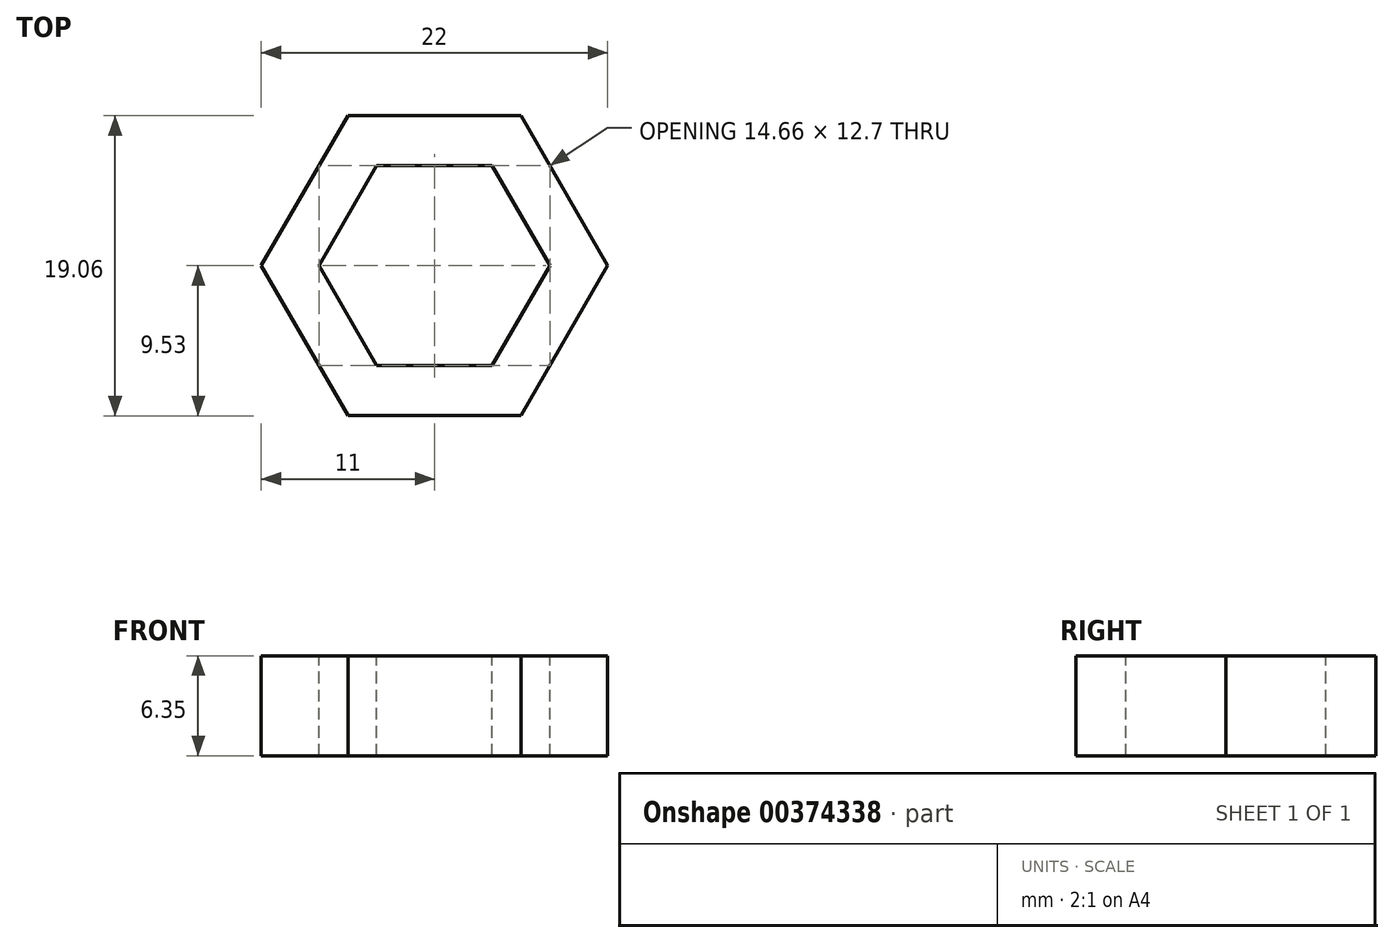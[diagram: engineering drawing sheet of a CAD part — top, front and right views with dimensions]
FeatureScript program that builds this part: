
annotation { "Feature Type Name" : "Feature", "Feature Type Description" : "" }
export const myFeature = defineFeature(function(context is Context, id is Id, definition is map)
    precondition{}
    {
        {
            var Q0;
            Q0=qCreatedBy(makeId("Top.planeOp"),FACE);
            cPlane(context, id + "F0", {"entities" : qUnion([Q0]), "cplaneType" : CPlaneType.OFFSET, "offset" : 38.1 * mm, "width" : 152.4 * mm, "height" : 152.4 * mm});
        }
        {
            var Q0;
            Q0=qCreatedBy(id+"F0.planeOp",FACE);
            var sketch = newSketch(context, id + "F1", { "sketchPlane" : qUnion([Q0])});
            skCircle(sketch, "E0.cCircle", {"center": v(0, 0) * mm, "radius": 9.53 * mm, "construction": true});
            skLineSegment(sketch, "E0.0", {"start": v(11, 0) * mm, "end": v(5.5, -9.53) * mm});
            skLineSegment(sketch, "E0.1", {"start": v(5.5, -9.53) * mm, "end": v(-5.5, -9.53) * mm});
            skLineSegment(sketch, "E0.2", {"start": v(-5.5, -9.53) * mm, "end": v(-11, 0) * mm});
            skLineSegment(sketch, "E0.3", {"start": v(-11, 0) * mm, "end": v(-5.5, 9.53) * mm});
            skLineSegment(sketch, "E0.4", {"start": v(-5.5, 9.53) * mm, "end": v(5.5, 9.53) * mm});
            skLineSegment(sketch, "E0.5", {"start": v(5.5, 9.52) * mm, "end": v(11, 0) * mm});
            skPoint(sketch, "E0.0.midPoint", {"position": v(8.25, -4.76) * mm});
            skSolve(sketch);
        }
        {
            var Q0;
            Q0 = qSketchRegion(id + "F1", true);
            extrude(context, id + "F2", {"entities" : qUnion([Q0]), "depth" : 6.35 * mm});
        }
        {
            var Q0;
            Q0=makeQuery(id+"F2.opExtrude","CAP_FACE",FACE,{"disambiguationData":[OSD([sQuery(id+"F1.wireOp",EDGE,"E0.0"),sQuery(id+"F1.wireOp",EDGE,"E0.1"),sQuery(id+"F1.wireOp",EDGE,"E0.2"),sQuery(id+"F1.wireOp",EDGE,"E0.3"),sQuery(id+"F1.wireOp",EDGE,"E0.4"),sQuery(id+"F1.wireOp",EDGE,"E0.5")])],"isStart":false});
            var sketch = newSketch(context, id + "F3", { "sketchPlane" : qUnion([Q0])});
            skCircle(sketch, "E1.cCircle", {"center": v(0, 0) * mm, "radius": 6.35 * mm, "construction": true});
            skLineSegment(sketch, "E1.0", {"start": v(7.33, 0) * mm, "end": v(3.67, -6.35) * mm});
            skLineSegment(sketch, "E1.1", {"start": v(3.67, -6.35) * mm, "end": v(-3.67, -6.35) * mm});
            skLineSegment(sketch, "E1.2", {"start": v(-3.67, -6.35) * mm, "end": v(-7.33, 0) * mm});
            skLineSegment(sketch, "E1.3", {"start": v(-7.33, 0) * mm, "end": v(-3.67, 6.35) * mm});
            skLineSegment(sketch, "E1.4", {"start": v(-3.67, 6.35) * mm, "end": v(3.67, 6.35) * mm});
            skLineSegment(sketch, "E1.5", {"start": v(3.67, 6.35) * mm, "end": v(7.33, 0) * mm});
            skPoint(sketch, "E1.0.midPoint", {"position": v(5.5, -3.18) * mm});
            skSolve(sketch);
        }
        {
            var Q0;
            Q0 = qSketchRegion(id + "F3", true);
            var Q1;
            Q1=sQuery(id+"F3.wireOp",EDGE,"E1.4");
            var Q2;
            Q2=sQuery(id+"F3.wireOp",EDGE,"E1.5");
            var Q3;
            Q3=sQuery(id+"F3.wireOp",EDGE,"E1.0");
            var Q4;
            Q4=sQuery(id+"F3.wireOp",EDGE,"E1.1");
            var Q5;
            Q5=sQuery(id+"F3.wireOp",EDGE,"E1.2");
            var Q6;
            Q6=sQuery(id+"F3.wireOp",EDGE,"E1.3");
            extrude(context, id + "F4", {"entities" : qUnion([Q0]), "operationType" : NewBodyOperationType.REMOVE, "surfaceEntities" : qUnion([Q1, Q2, Q3, Q4, Q5, Q6]), "oppositeDirection" : true, "depth" : 6.35 * mm});
        }
        {
            var Q0;
            Q0=makeQuery(id+"FWYhQ1iWhGToiTQ_1.imprint","IMPRINT",FACE,{"disambiguationData":[TD([[makeQuery(id+"FWYhQ1iWhGToiTQ_1.imprint","IMPRINT",EDGE,{"derivedFrom":sQuery(id+"FWYhQ1iWhGToiTQ_1.wireOp",EDGE,"xiZl9O74-YZky-L7WO-wjCw-sWpObsmwQ9eS")}),1.0]])]});
            var sketch = newSketch(context, id + "F5", { "sketchPlane" : qUnion([Q0])});
            skCircle(sketch, "E2", {"center": v(0, 0) * mm, "radius": 12.7 * mm});
            skSolve(sketch);
        }
        {
            var Q0;
            Q0=qCreatedBy(makeId("Top.planeOp"),FACE);
            cPlane(context, id + "F6", {"entities" : qUnion([Q0]), "cplaneType" : CPlaneType.OFFSET, "offset" : 6.35 * mm, "width" : 152.4 * mm, "height" : 152.4 * mm});
        }
    });
